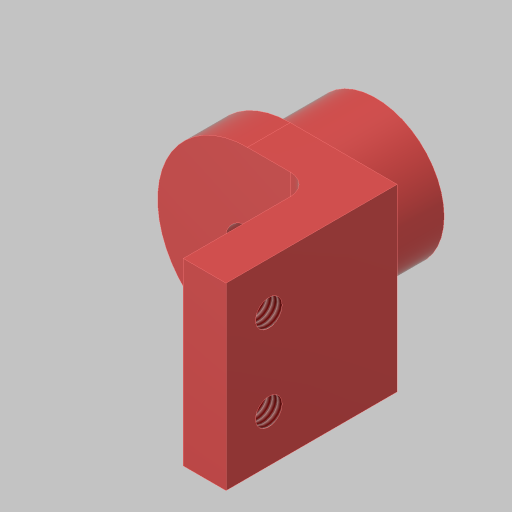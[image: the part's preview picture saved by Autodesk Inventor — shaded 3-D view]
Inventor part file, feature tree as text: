
AUTODESK INVENTOR PART (.ipt)
format: ipt  version: 2023.5 (Build 275446000, 446)  size: 151,040 bytes
history: native  units: in
note: dims shown in document units (in); Inventor stores cm internally (conversion verified against a paired STEP export)
features: sketch x5, extrude x3, hole x2, fillet x1, projected_geometry x1
ambient origin geometry x8: Origin, YZ Plane, XZ Plane, XY Plane, X Axis, Y Axis, Z Axis, Center Point
bodies: Solid1 (feature_tree)
feature tree (12):
  extrude  "Extrusion1"  Depth=0.5in TaperAngle=0.0deg
  extrude  "Extrusion2"  Depth=0.25in TaperAngle=0.0deg
  hole  "Hole2"  [1 undecoded]
  extrude  "Extrusion3"  Depth=0.25in
  fillet  "Fillet1"  Radius=0.75in
  hole  "Hole3"  [1 undecoded]
  sketch  "Sketch1"  dims[d0=0.8in d1=0.5in d2=0.0in]
  sketch  "Sketch2"  dims[d3=0.125in d4=0.25in d5=0.0in]
  sketch  "Sketch4"  dims[d6=0.688in d14=0.625in]
  sketch  "Sketch5"  dims[d15=0.257in d16=0.75in d17=0.375in d18=0.25in d19=0.5635in d20=1.0in d21=0.8108in d22=0.25in d23=0.75in d24=0.0in]
  sketch  "Sketch6"  dims[d25=0.125in d26=0.5in d27=0.156in d28=0.38in d29=0.385in d30=0.25in d31=0.5635in d32=1.0in d33=0.8108in d34=0.25in]
  projected_geometry  "Project Cut Edges1"
note: 2 required parameter values undecoded (feature->parameter linkage not recoverable at this tier; creation-order binding heuristic only, values carry confidence <= 0.55)
